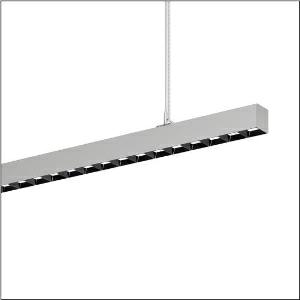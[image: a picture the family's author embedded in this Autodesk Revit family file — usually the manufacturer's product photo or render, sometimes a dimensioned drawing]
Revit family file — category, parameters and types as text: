
# Revit family: silica_r__21_51mx32tat7s_c957
name_source: partatom
category: Lighting Fixtures
units: mm (PartAtom-declared; Revit-internal decimal feet)

## family parameters
Cut with Voids When Loaded = No
Host = Face
Light Source = No
Part Type = Normal
Room Calculation Point = No
Round Connector Dimension = Use Diameter
Shared = No

## types (1)
- --- (1 x LED, 6220 lm, 53.4 W, 6500K)
    Apparent Load = 53 VA
    CIE Flux Codes = 84 99 100 60 100
    Color Rendering = 80
    Color Temperature = 6500K
    Default Elevation = 1800 mm
    Description = Silica® 21, office luminaire, primary light control with darklight reflector, of PMMA, black, CAT 2 (L<= 3000cd/m²), light emission: direct/indirect distribution, primary light characteristic: symmetric, installation type: suspended mounting, LED, rated luminous flux: 6.220lm, luminous efficacy: 111lm/W, light colour: 8tw, colour temperature: 2700..6500K, control gear: ECG DALI, with terminal, 3+2-pole, max. 2.5mm², mains connection: 220..240V, AC, 50/60Hz, rated input power: 56.1W, luminaire housing, of aluminium, metallic grey (RAL 9006), length: 1.204mm, width: 53mm, height: 53mm, protection rating (complete): IP20, insulation class (complete): insulation class I (protective earthing), certification: CE, permissible operating ambient temperature: 0..+35°C, standard: EN 50419, packaging unit: 1 piece
    Height = 53 mm
    Lamp = 1 x LED
    Lamp Light Flux = 6220 lm
    Lamp Power = 53.4 W
    Lamp count = 1
    Length = 1204 mm
    Luminous efficacy = 116 lm/W
    Manufacturer = Siteco
    ModVariant = No
    Model = 51MX32TAT7S
    Mounting Place = Ceiling
    Mounting Type = Pendant
    Number of Poles = 1
    OnlyDefault = Yes
    Power Factor = 1
    Product Name = Silica® 21
    Product group = office luminaire | ceiling pendant
    ProductGroupID = 902
    Protection Class = Protection class I
    Protection Degree = IP 20
    RLX_Detail_Level = 1
    RLX_Emergency_Light_Flux = 0 lm
    RLX_Emergency_Type = 0
    RLX_Emergency_Type_DB = No
    RlxData = <blob elided: 41233 chars, md5=6e7f4011>
    Socket = socket
    Standby Power = 0 W
    System Light Flux = 6220 lm
    System Power = 53 W
    Type Comments = individual setting
    Type Image = l_1297751.jpg
    URL = http://relux.com
    VarID = @adj_071251
    Voltage = 0 V
    Weight = 0.00 kg
    Width = 53 mm

## geometry (parser evidence)
native form markers: Blend x4, Sweep x13
no freeform markers — native parametric forms only
